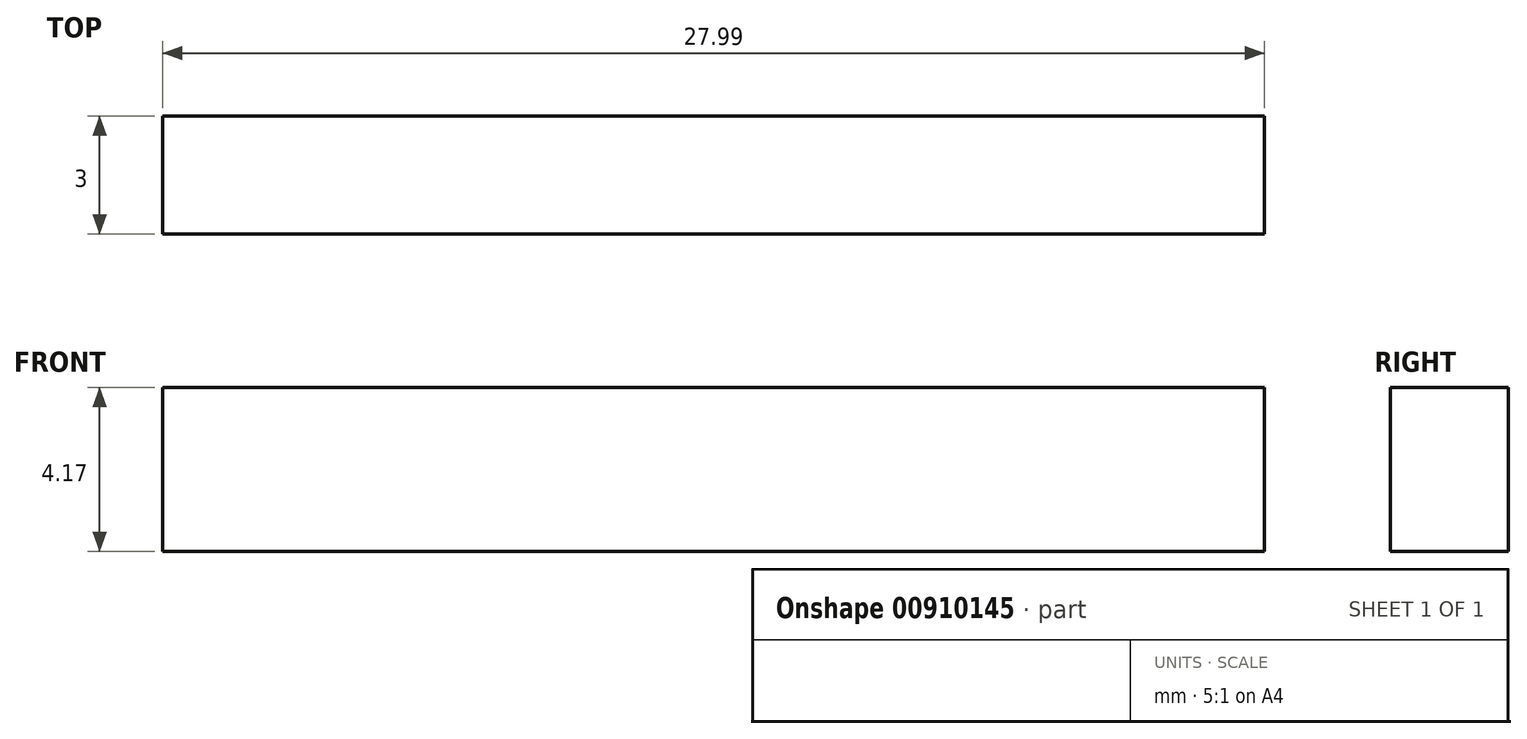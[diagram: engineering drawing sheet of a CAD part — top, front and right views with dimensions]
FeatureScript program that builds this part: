
annotation { "Feature Type Name" : "Feature", "Feature Type Description" : "" }
export const myFeature = defineFeature(function(context is Context, id is Id, definition is map)
    precondition{}
    {
        {
            var Q0;
            Q0=qCreatedBy(makeId("Front.planeOp"),FACE);
            var sketch = newSketch(context, id + "F0", { "sketchPlane" : qUnion([Q0])});
            skLineSegment(sketch, "E0.bottom", {"start": v(-64.01, 21.04) * mm, "end": v(-36.02, 21.04) * mm});
            skLineSegment(sketch, "E0.top", {"start": v(-64.01, 16.87) * mm, "end": v(-36.02, 16.87) * mm});
            skLineSegment(sketch, "E0.left", {"start": v(-64.01, 21.04) * mm, "end": v(-64.01, 16.87) * mm});
            skLineSegment(sketch, "E0.right", {"start": v(-36.02, 21.04) * mm, "end": v(-36.02, 16.87) * mm});
            skSolve(sketch);
        }
        {
            var Q0;
            Q0=makeQuery(id+"F0.imprint","IMPRINT",FACE,{"disambiguationData":[TD([[makeQuery(id+"F0.imprint","IMPRINT",EDGE,{"derivedFrom":sQuery(id+"F0.wireOp",EDGE,"E0.bottom")}),-1.0]])]});
            var Q1;
            Q1 = qConstructionFilter(qBodyType(qCreatedBy(id + "F0" ,EDGE), BodyType.WIRE), ConstructionObject.NO);
            extrude(context, id + "F1", {"entities" : qUnion([Q0]), "surfaceEntities" : qUnion([Q1]), "depth" : 3 * mm, "offsetDistance" : 25 * mm});
        }
    });
